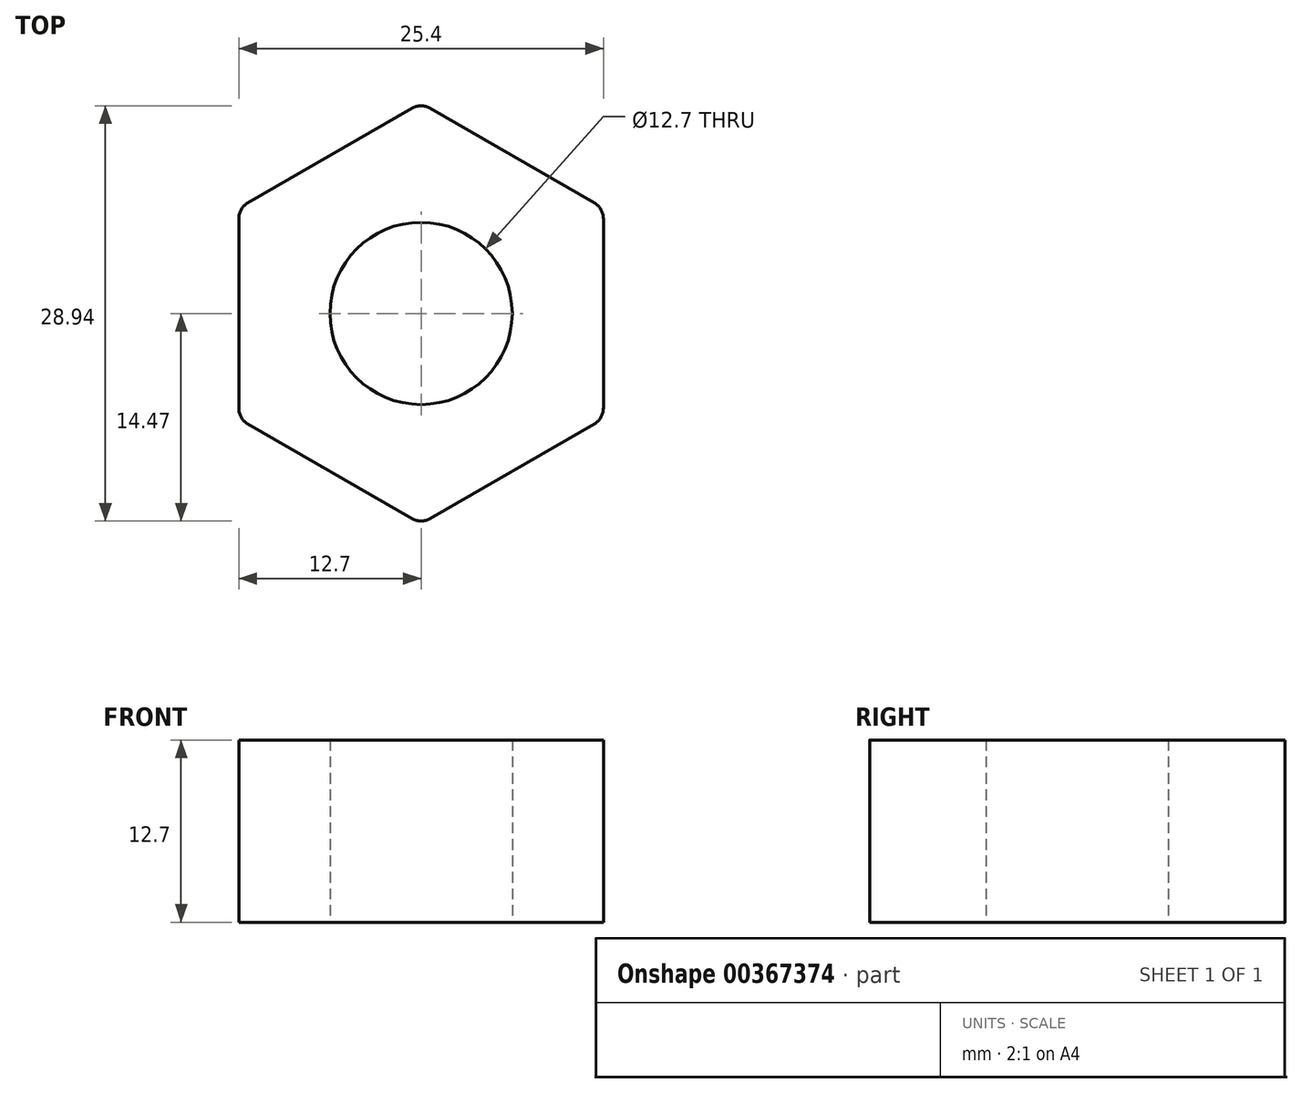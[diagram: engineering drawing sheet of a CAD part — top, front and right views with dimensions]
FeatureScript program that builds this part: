
annotation { "Feature Type Name" : "Feature", "Feature Type Description" : "" }
export const myFeature = defineFeature(function(context is Context, id is Id, definition is map)
    precondition{}
    {
        {
            var Q0;
            Q0=qCreatedBy(makeId("Top.planeOp"),FACE);
            var sketch = newSketch(context, id + "F0", { "sketchPlane" : qUnion([Q0])});
            skCircle(sketch, "E0", {"center": v(0, 0) * mm, "radius": 12.7 * mm});
            skLineSegment(sketch, "E1", {"start": v(-12.7, 7.33) * mm, "end": v(-12.7, -7.33) * mm});
            skLineSegment(sketch, "E2", {"start": v(-12.7, -7.33) * mm, "end": v(0, -14.66) * mm});
            skLineSegment(sketch, "E3", {"start": v(0, -14.66) * mm, "end": v(12.7, -7.33) * mm});
            skLineSegment(sketch, "E4", {"start": v(12.7, -7.33) * mm, "end": v(12.7, 7.33) * mm});
            skLineSegment(sketch, "E5", {"start": v(12.7, 7.33) * mm, "end": v(0, 14.66) * mm});
            skLineSegment(sketch, "E6", {"start": v(0, 14.66) * mm, "end": v(-12.7, 7.33) * mm});
            skCircle(sketch, "E7", {"center": v(0, 0) * mm, "radius": 6.35 * mm});
            skSolve(sketch);
        }
        {
            var Q0;
            Q0 = qSketchRegion(id + "F0", true);
            extrude(context, id + "F1", {"entities" : qUnion([Q0]), "depth" : 12.7 * mm});
        }
        {
            var Q0;
            Q0=makeQuery(id+"F1.opExtrude","SWEPT_EDGE",EDGE,{"disambiguationData":[OSD([sQuery(id+"F0.wireOp",EDGE,"E1"),sQuery(id+"F0.wireOp",EDGE,"E2")])]});
            var Q1;
            Q1=makeQuery(id+"F1.opExtrude","SWEPT_EDGE",EDGE,{"disambiguationData":[OSD([sQuery(id+"F0.wireOp",EDGE,"E2"),sQuery(id+"F0.wireOp",EDGE,"E3")])]});
            var Q2;
            Q2=makeQuery(id+"F1.opExtrude","SWEPT_EDGE",EDGE,{"disambiguationData":[OSD([sQuery(id+"F0.wireOp",EDGE,"E3"),sQuery(id+"F0.wireOp",EDGE,"E4")])]});
            var Q3;
            Q3=makeQuery(id+"F1.opExtrude","SWEPT_EDGE",EDGE,{"disambiguationData":[OSD([sQuery(id+"F0.wireOp",EDGE,"E4"),sQuery(id+"F0.wireOp",EDGE,"E5")])]});
            var Q4;
            Q4=makeQuery(id+"F1.opExtrude","SWEPT_EDGE",EDGE,{"disambiguationData":[OSD([sQuery(id+"F0.wireOp",EDGE,"E5"),sQuery(id+"F0.wireOp",EDGE,"E6")])]});
            var Q5;
            Q5=makeQuery(id+"F1.opExtrude","SWEPT_EDGE",EDGE,{"disambiguationData":[OSD([sQuery(id+"F0.wireOp",EDGE,"E1"),sQuery(id+"F0.wireOp",EDGE,"E6")])]});
            fillet(context, id + "F2", {"entities" : qUnion([Q0, Q1, Q2, Q3, Q4, Q5]), "radius" : 1.27 * mm, "tangentPropagation" : true, "allowEdgeOverflow" : false});
        }
    });
